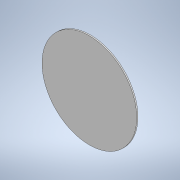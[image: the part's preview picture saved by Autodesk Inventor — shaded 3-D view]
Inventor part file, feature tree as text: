
AUTODESK INVENTOR PART (.ipt)
format: ipt  version: 2020 (Build 240168000, 168)  size: 106,496 bytes
history: native  units: in
note: dims shown in document units (in); Inventor stores cm internally (conversion verified against a paired STEP export)
features: extrude x1, sketch x1
ambient origin geometry x8: Origin, YZ Plane, XZ Plane, XY Plane, X Axis, Y Axis, Z Axis, Center Point
bodies: Solid1 (feature_tree)
feature tree (2):
  extrude  "Extrusion1"  Depth=0.1575in TaperAngle=0.0deg
  sketch  "Sketch1"  dims[d0=11.811in d1=0.1575in d2=0.0in d3=0.0197in d4=0.0344in]
